# Revit family: FP-Revit20-en-DD60DTX6HI1_CN-DishDrawer-0-90003896A-CN
name_source: partatom
category: Specialty Equipment
units: mm (PartAtom-declared; Revit-internal decimal feet)

## family parameters
Always vertical = Yes
Cut with Voids When Loaded = Yes
OmniClass Number = 23.40.40.14.31
OmniClass Title = Cleaning and Disposal Equipment
Part Type = Normal
Room Calculation Point = No
Round Connector Dimension = Use Diameter
Shared = No
Work Plane-Based = No

## types (1)
- DD60DTX6HI1_CN
    Cavity - Depth (excluding front panel) = 560 mm  [stored 1.83727 ft]
    Cavity - Width = 600 mm  [stored 1.9685 ft]
    Chassis - Depth = 553 mm  [stored 1.8143 ft]
    Chassis - Height = 855 mm  [stored 2.80512 ft]
    Connector Description - Electrical = 220-240 V, 50 Hz, min 8.5 A, fused electrical supply
    Connector Description - Sanitary = Drain Hose, No Fitting Required
    Connector Description - Water = 3/4” BSP (GB20) to suit flat washer
    Default Elevation = 0 mm  [stored 0 ft]
    Description = 60cm DishDrawer, Integrated
    Manufacturer = Fisher & Paykel Appliances
    Material - Body = Fisher & Paykel - Grey
    Material - Front = Fisher & Paykel - Stainless Steel
    Material - Toe Kick = Fisher & Paykel - Stainless Steel
    Material - Trim = Fisher & Paykel - Black
    Model = DD60DTX6HI1_CN
    Product - Depth = 571 mm  [stored 1.87336 ft]
    Product - Width = 599 mm  [stored 1.96522 ft]
    URL = www.fisherpaykel.com
    Visibility - Clearance Required = Yes
    Visibility - Door Panel = No
    Visibility - Toe Kick = No

note: [stored X ft] marks values corroborated as IEEE doubles in the binary element streams (Revit-internal decimal feet)

## geometry (parser evidence)
native form markers: Sweep x5
no freeform markers — native parametric forms only
